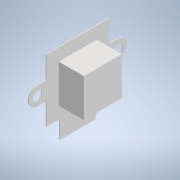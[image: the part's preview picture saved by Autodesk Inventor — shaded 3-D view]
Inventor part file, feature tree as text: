
AUTODESK INVENTOR PART (.ipt)
format: ipt  version: 2022 (Build 260153000, 153)  size: 136,704 bytes
history: native  units: mm
features: extrude x2, sketch x2, other x1
ambient origin geometry x8: Origin, YZ Plane, XZ Plane, XY Plane, X Axis, Y Axis, Z Axis, Center Point
bodies: Body1 (feature_tree)
feature tree (5):
  other  "Твердое тело1"
  extrude  "Выдавливание1"  Depth=14.0mm
  extrude  "Выдавливание2"  Depth=14.0mm
  sketch  "Эскиз1"
  sketch  "Эскиз2"
